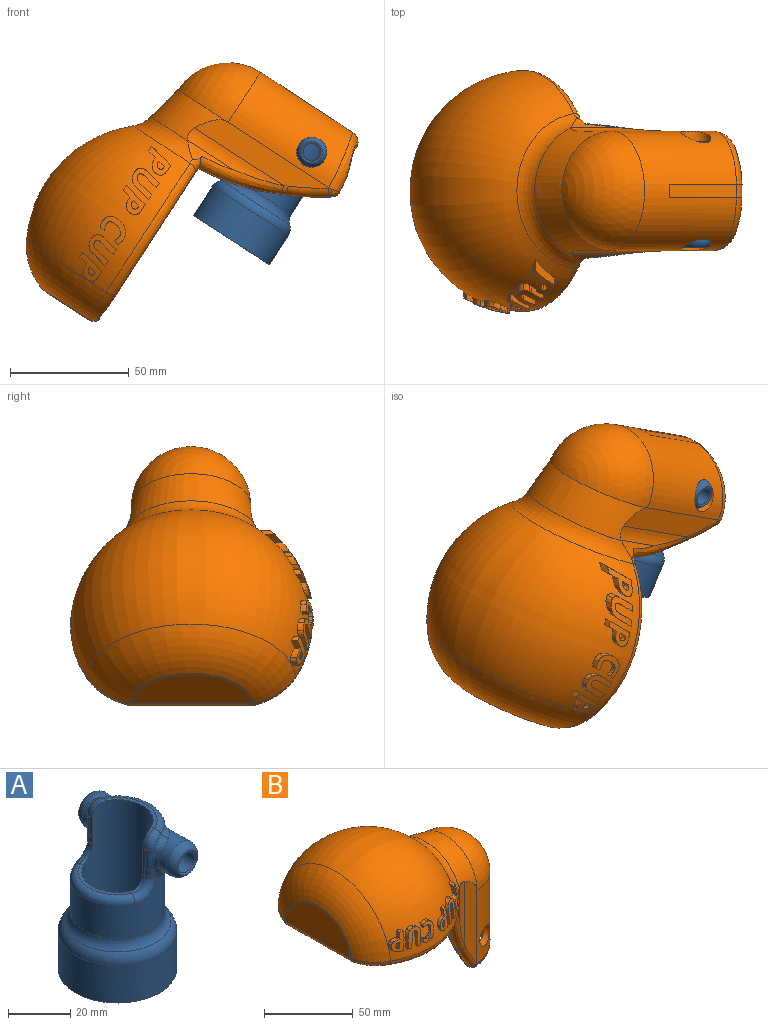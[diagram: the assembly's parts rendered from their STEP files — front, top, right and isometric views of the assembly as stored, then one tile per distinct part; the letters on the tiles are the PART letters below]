
ASSEMBLY  parts=2 mates=1
PART A: 61 faces, bbox 44.5x46.1x59 mm
  f0: cylinder r=6.35mm len=12.96mm, axis (0,1,0), area 175.7mm2, adj f33,f34,f35,f36,f37,f38,f39,f59
  f1: plane 27.88x27.32mm, normal (0,0,-1), area 165.8mm2, adj f3,f45,f47,f53,f54,f55
  f2: cylinder r=15.24mm len=33.18mm, axis (0,0,1), area 1735mm2, adj f14,f23,f24,f25,f26,f35,f50
  f3: cylinder r=11.43mm len=45.72mm, axis (0,0,1), area 2553.8mm2, adj f1,f4,f5,f6,f7,f10,f11,f12
  f4: plane 23.28x7.62mm, normal (0,0,1), area 34.8mm2, adj f3,f10,f11,f25
  f5: plane 23.28x7.62mm, normal (0,0,1), area 34.8mm2, adj f3,f12,f13,f14
  f6: plane 10.16x1.25mm, normal (-1,0,0), area 11.2mm2, adj f3,f11,f13,f18,f20,f22
  f7: plane 10.16x1.25mm, normal (-1,0,0), area 11.2mm2, adj f3,f10,f12,f17,f19,f21
  f8: cylinder r=6.35mm len=15.41mm, axis (0,-1,0), area 273.5mm2, adj f9,f26,f27,f28,f29,f30,f31,f32
  f9: torus R=2.54mm, axis (0,-1,0), area 137.8mm2, adj f8,f43
  f10: cylinder r=5.08mm len=5.08mm, axis (0,1,0), area 10.5mm2, adj f3,f4,f7,f23
  f11: cylinder r=5.08mm len=5.08mm, axis (0,1,0), area 10.5mm2, adj f3,f4,f6,f24
  f12: cylinder r=5.08mm len=5.08mm, axis (0,-1,0), area 7mm2, adj f3,f5,f7,f15
  f13: cylinder r=5.08mm len=5.08mm, axis (0,-1,0), area 7mm2, adj f3,f5,f6,f16
  f14: torus R=12.7mm, axis (0,0,-1), area 118.5mm2, adj f2,f5,f15,f16,f27,f33
  f15: bspline ~7.3x6.43mm, area 22.4mm2, adj f12,f14,f17,f34
  f16: bspline ~7.3x6.43mm, area 22.4mm2, adj f13,f14,f18,f29
  f17: cylinder r=2.54mm len=2.26mm, axis (0,0,1), area 0.7mm2, adj f7,f15,f19,f36
  f18: cylinder r=2.54mm len=2.26mm, axis (0,0,1), area 0.7mm2, adj f6,f16,f20,f31
  f19: bspline ~9x3.71mm, area 16.6mm2, adj f7,f17,f21,f38
  f20: bspline ~9x3.71mm, area 16.6mm2, adj f6,f18,f22,f32
  f21: cylinder r=2.54mm len=2.52mm, axis (0,0,1), area 7.9mm2, adj f7,f19,f23,f39
  f22: cylinder r=2.54mm len=2.52mm, axis (0,0,1), area 7.9mm2, adj f6,f20,f24,f30
  f23: bspline ~10.2x9.31mm, area 41.7mm2, adj f2,f10,f21,f25,f37
  f24: bspline ~10.2x9.31mm, area 41.7mm2, adj f2,f11,f22,f25,f28
  f25: torus R=12.7mm, axis (0,0,1), area 132.4mm2, adj f2,f4,f23,f24
  f26: bspline ~15.78x13.42mm, area 65mm2, adj f2,f8,f27,f28
  f27: bspline ~7.77x7.33mm, area 19.7mm2, adj f8,f14,f26,f29
  f28: bspline ~3.6x3.31mm, area 5mm2, adj f8,f24,f26,f30
  f29: bspline ~6.56x5.39mm, area 19.2mm2, adj f8,f16,f27,f31
  f30: bspline ~5.56x3.31mm, area 7.5mm2, adj f8,f22,f28,f32
  f31: bspline ~3.18x2.71mm, area 0.6mm2, adj f8,f18,f29,f32
  f32: bspline ~7.72x2.3mm, area 15.4mm2, adj f8,f20,f30,f31
  f33: bspline ~7.77x7.33mm, area 19.7mm2, adj f0,f14,f34,f35
  f34: bspline ~6.54x5.29mm, area 19.2mm2, adj f0,f15,f33,f36
  f35: bspline ~15.78x13.42mm, area 65mm2, adj f0,f2,f33,f37
  f36: bspline ~2.47x2.11mm, area 0.6mm2, adj f0,f17,f34,f38
  f37: bspline ~3.89x3.5mm, area 5mm2, adj f0,f23,f35,f39
  f38: bspline ~7.43x2.28mm, area 15.4mm2, adj f0,f19,f36,f39
  f39: bspline ~4.81x2.98mm, area 7.5mm2, adj f0,f21,f37,f38
  f40: cylinder r=15.24mm len=7.11mm, axis (0,0,1), area 47mm2, adj f42
  f41: cylinder r=3.81mm len=10.03mm, axis (0,-1,0), area 240.1mm2, adj f42,f43
  f42: bspline ~7.63x7.63mm, area 11.2mm2, adj f40,f41
  f43: torus R=4.32mm, axis (0,1,0), area 28.1mm2, adj f9,f41
  f44: cylinder r=14.02mm len=28.04mm, axis (0,0,1), area 244.3mm2, adj f46,f49,f52,f54
  f45: cylinder r=14.02mm len=28.04mm, axis (0,0,1), area 170.8mm2, adj f1,f46,f47,f53,f54
  f46: cylinder r=14.02mm len=28.04mm, axis (0,0,1), area 175.5mm2, adj f44,f45,f53,f54
  f47: cylinder r=14.02mm len=19.54mm, axis (0,0,1), area 18.5mm2, adj f1,f45,f53
  f48: cylinder r=19.05mm len=38.1mm, axis (0,0,1), area 1767.6mm2, adj f49,f51
  f49: plane 38.1x38.1mm, normal (0,0,-1), area 522.5mm2, adj f44,f48
  f50: torus R=20.32mm, axis (0,0,-1), area 454.3mm2, adj f2,f51
  f51: torus R=13.97mm, axis (0,0,-1), area 526mm2, adj f48,f50
  f52: plane 2.27x1.59mm, normal (0,-1,0), area 2.1mm2, adj f44,f53,f54,f55
  f53: bspline ~32.61x28.25mm, area 325.2mm2, adj f1,f45,f46,f47,f52,f55
  f54: bspline ~32.61x28.25mm, area 359.2mm2, adj f1,f44,f45,f46,f52,f55
  f55: bspline ~25.33x25.33mm, area 163.2mm2, adj f1,f52,f53,f54
  f56: cylinder r=15.24mm len=7.11mm, axis (0,0,1), area 47.1mm2, adj f57
  f57: bspline ~7.64x7.63mm, area 11.2mm2, adj f56,f58
  f58: cylinder r=3.81mm len=8.34mm, axis (0,1,0), area 199.5mm2, adj f57,f60
  f59: torus R=2.54mm, axis (0,1,0), area 137.8mm2, adj f0,f60
  f60: torus R=4.32mm, axis (0,-1,0), area 28.1mm2, adj f58,f59
PART B: 217 faces, bbox 157.1x102.9x107 mm
  f0: plane 67.87x24.74mm, normal (0,0,-1), area 166.8mm2, adj f145,f161,f174,f175,f176,f177,f188
  f1: cylinder r=81.7mm len=2.3mm, axis (0,1,0), area 0.2mm2, adj f153,f165,f194
  f2: cylinder r=81.7mm len=2.3mm, axis (0,1,0), area 0.2mm2, adj f151,f160,f202
  f3: revolved ~57.08x28.54mm, area 1079.3mm2, adj f4,f8,f10,f22,f146,f147,f148,f149
  f4: torus R=41.02mm, axis (1,0,0), area 709.4mm2, adj f3,f17,f146,f147,f168,f176
  f5: cylinder r=95.28mm len=36.91mm, axis (0,1,0), area 88.7mm2, adj f7,f155,f156,f189,f211,f212,f213,f216
  f6: plane 7.45x0.22mm, normal (0,0,-1), area 0.4mm2, adj f18,f190,f204,f214,f216
  f7: plane 67.88x24.74mm, normal (0,0,-1), area 166.8mm2, adj f5,f155,f168,f169,f170,f187,f189
  f8: plane 61.06x9.66mm, normal (0,1,0), area 482.8mm2, adj f3,f23,f148,f150,f156,f157
  f9: cylinder r=97.33mm len=16.92mm, axis (0,1,0), area 28.3mm2, adj f156,f157,f158,f159,f160,f204,f216
  f10: plane 61.05x9.66mm, normal (0,-1,0), area 482.8mm2, adj f3,f23,f149,f154,f162,f163
  f11: plane 23.45x18.02mm, normal (0,1,0), area 220.5mm2, adj f20,f26,f30,f140,f142,f191,f192,f193
  f12: cylinder r=97.33mm len=16.92mm, axis (0,1,0), area 28.3mm2, adj f162,f163,f164,f165,f166,f192,f210
  f13: plane 49.16x23.02mm, normal (1,0,0), area 873.9mm2, adj f139,f182
  f14: plane 51.98x22.46mm, normal (-1,0,0), area 884.5mm2, adj f167,f172
  f15: revolved ~87.08x61.63mm, area 8180.4mm2, adj f35,f139,f177,f178,f186,f187,f188,f189
  f16: plane 3.03x1.98mm, normal (-1,0,0), area 4.5mm2, adj f17,f81,f82,f114
  f17: revolved ~101.51x64.76mm, area 9394.4mm2, adj f4,f16,f37,f38,f39,f40,f41,f42
  f18: plane 23.45x18.02mm, normal (0,-1,0), area 220.5mm2, adj f6,f19,f25,f34,f143,f190,f201,f202
  f19: cylinder r=18.64mm len=7.12mm, axis (-1,0,0), area 25.2mm2, adj f18,f21,f25,f33
  f20: cylinder r=18.64mm len=7.12mm, axis (-1,0,0), area 25.2mm2, adj f11,f21,f26,f31
  f21: cylinder r=18.64mm len=37.28mm, axis (0,0,-1), area 1116.5mm2, adj f19,f20,f24,f32,f142,f143
  f22: sphere r=25.17mm, area 1990.7mm2, adj f3,f23
  f23: cylinder r=25.17mm len=50.39mm, axis (0,0,-1), area 3341.1mm2, adj f8,f10,f22,f25,f26,f27,f28,f151
  f24: sphere r=18.64mm, area 1091.3mm2, adj f21,f36
  f25: cylinder r=6.35mm len=12.7mm, axis (0,1,0), area 210.8mm2, adj f18,f19,f23,f33,f34
  f26: cylinder r=6.35mm len=12.7mm, axis (0,1,0), area 210.8mm2, adj f11,f20,f23,f30,f31
  f27: cylinder r=18.64mm len=5.71mm, axis (-1,0,0), area 0mm2, adj f23,f28
  f28: cylinder r=65.2mm len=33.92mm, axis (0,0,-1), area 193.1mm2, adj f23,f27,f151,f152,f153
  f29: cylinder r=51.61mm len=31.32mm, axis (0,0,-1), area 420.4mm2, adj f30,f31,f32,f33,f34,f197,f198,f199
  f30: cylinder r=12.7mm len=22.38mm, axis (0,0,-1), area 285.7mm2, adj f11,f26,f29,f31,f196
  f31: bspline ~12.67x11.58mm, area 94.4mm2, adj f20,f26,f29,f30,f32
  f32: bspline ~38.72x19.54mm, area 417.7mm2, adj f21,f29,f31,f33
  f33: bspline ~12.68x11.68mm, area 94.4mm2, adj f19,f25,f29,f32,f34
  f34: cylinder r=12.7mm len=22.38mm, axis (0,0,-1), area 285.7mm2, adj f18,f25,f29,f33,f200
  f35: torus R=38.79mm, axis (1,0,0), area 1101.1mm2, adj f15,f36,f141,f144,f188,f189,f205,f211
  f36: torus R=105.72mm, axis (1,0,0), area 1155mm2, adj f24,f35,f142,f143
  f37: torus R=19.04mm, axis (-1,0,0), area 2380.3mm2, adj f17,f170,f172,f174
  f38: extruded ~2.62x2.43mm, area 6.9mm2, adj f17,f39,f46,f117
  f39: extruded ~4.35x2.78mm, area 7.7mm2, adj f17,f38,f40,f117
  f40: plane 4.89x2.6mm, normal (0,0,-1), area 7.2mm2, adj f17,f39,f41,f117
  f41: plane 11.41x11.13mm, normal (0.98,0,-0.21), area 42.4mm2, adj f17,f40,f42,f117
  f42: plane 6.98x2.4mm, normal (0,0,1), area 10.4mm2, adj f17,f41,f43,f117
  f43: plane 6.77x3.99mm, normal (-0.98,0,0.2), area 15.7mm2, adj f17,f42,f44,f117
  f44: plane 4.09x0.66mm, normal (0,0,1), area 2.3mm2, adj f17,f43,f45,f117
  f45: extruded ~6.38x3.56mm, area 12.3mm2, adj f17,f44,f46,f117
  f46: extruded ~4.62x2.88mm, area 9.1mm2, adj f17,f38,f45,f117
  f47: plane 2.74x2.34mm, normal (0,0,-1), area 4.4mm2, adj f17,f48,f61,f116
  f48: plane 7.01x4.77mm, normal (0.98,0,-0.21), area 15.6mm2, adj f17,f47,f49,f116
  f49: extruded ~3.61x1.74mm, area 5mm2, adj f17,f48,f50,f116
  f50: extruded ~3.72x1.48mm, area 4.5mm2, adj f17,f49,f51,f116
  f51: extruded ~3x1.44mm, area 6.3mm2, adj f17,f50,f52,f116
  f52: extruded ~3.17x0.95mm, area 2.6mm2, adj f17,f51,f53,f116
  f53: plane 7.03x5.17mm, normal (-0.98,0,0.21), area 16.9mm2, adj f17,f52,f54,f116
  f54: plane 3.34x2.34mm, normal (0,0,-1), area 4.9mm2, adj f17,f53,f55,f116
  f55: plane 7.07x5.5mm, normal (0.98,0,-0.21), area 18mm2, adj f17,f54,f56,f116
  f56: extruded ~3.4x1.05mm, area 3.1mm2, adj f17,f55,f57,f116
  f57: extruded ~3.52x2.34mm, area 7.9mm2, adj f17,f56,f58,f116
  f58: extruded ~4.11x2.54mm, area 8.4mm2, adj f17,f57,f59,f116
  f59: extruded ~4.92x3.19mm, area 9.8mm2, adj f17,f58,f60,f116
  f60: extruded ~4.48x3.05mm, area 9mm2, adj f17,f59,f61,f116
  f61: plane 7.23x4.66mm, normal (-0.98,0,0.21), area 15.5mm2, adj f17,f47,f60,f116
  f62: extruded ~2.43x2.17mm, area 4.8mm2, adj f17,f63,f70,f115
  f63: extruded ~2.78x2.12mm, area 5.1mm2, adj f17,f62,f64,f115
  f64: plane 2.58x2.41mm, normal (0,0,-1), area 4.5mm2, adj f17,f63,f65,f115
  f65: plane 11.2x6.53mm, normal (0.98,0,-0.21), area 24.8mm2, adj f17,f64,f66,f115
  f66: plane 3.4x2.34mm, normal (0,0,1), area 6mm2, adj f17,f65,f67,f115
  f67: plane 4.21x3.97mm, normal (-0.98,0,0.2), area 9.7mm2, adj f17,f66,f68,f115
  f68: plane 2.4x0.66mm, normal (0,0,1), area 1.5mm2, adj f17,f67,f69,f115
  f69: extruded ~3.56x3.28mm, area 8.1mm2, adj f17,f68,f70,f115
  f70: extruded ~2.99x2.88mm, area 6.4mm2, adj f17,f62,f69,f115
  f71: extruded ~1.82x1.04mm, area 1.8mm2, adj f17,f72,f87,f114
  f72: extruded ~2x1.33mm, area 2.6mm2, adj f17,f71,f73,f114
  f73: plane 2.03x1.91mm, normal (-0.9,0,0.43), area 3.6mm2, adj f17,f72,f74,f114
  f74: extruded ~1.92x1.58mm, area 2.8mm2, adj f17,f73,f75,f114
  f75: extruded ~1.75x1.69mm, area 2.7mm2, adj f17,f74,f76,f114
  f76: extruded ~3.04x1.71mm, area 5.2mm2, adj f17,f75,f77,f114
  f77: extruded ~2.55x2.33mm, area 5.8mm2, adj f17,f76,f78,f114
  f78: extruded ~3.67x3.01mm, area 7.3mm2, adj f17,f77,f79,f114
  f79: extruded ~3.27x3.22mm, area 7.5mm2, adj f17,f78,f80,f114
  f80: extruded ~3x2.75mm, area 7.7mm2, adj f17,f79,f81,f114
  f81: extruded ~3.04x2.44mm, area 7.3mm2, adj f16,f17,f80,f114
  f82: extruded ~2.57x2.28mm, area 5.8mm2, adj f16,f17,f83,f114
  f83: extruded ~2.43x1.66mm, area 4mm2, adj f17,f82,f84,f114
  f84: extruded ~2.74x1.89mm, area 4.2mm2, adj f17,f83,f85,f114
  f85: extruded ~2.71x2.57mm, area 5.1mm2, adj f17,f84,f86,f114
  f86: extruded ~2.24x1.81mm, area 4.1mm2, adj f17,f85,f87,f114
  f87: extruded ~1.81x1.8mm, area 3.4mm2, adj f17,f71,f86,f114
  f88: plane 2.51x2.34mm, normal (0,0,-1), area 4.2mm2, adj f17,f89,f102,f113
  f89: plane 6.99x3.43mm, normal (0.98,0,-0.21), area 14.1mm2, adj f17,f88,f90,f113
  f90: extruded ~2.68x1.74mm, area 4.3mm2, adj f17,f89,f91,f113
  f91: extruded ~2.42x1.48mm, area 3.8mm2, adj f17,f90,f92,f113
  f92: extruded ~3.03x1.44mm, area 5.1mm2, adj f17,f91,f93,f113
  f93: extruded ~2.46x0.95mm, area 2.1mm2, adj f17,f92,f94,f113
  f94: plane 7.01x3.43mm, normal (-0.98,0,0.21), area 13.6mm2, adj f17,f93,f95,f113
  f95: plane 2.33x2.1mm, normal (0,0,-1), area 3.9mm2, adj f17,f94,f96,f113
  f96: plane 7.04x3.46mm, normal (0.98,0,-0.21), area 13.4mm2, adj f17,f95,f97,f113
  f97: extruded ~2.47x1.05mm, area 2.2mm2, adj f17,f96,f98,f113
  f98: extruded ~3.28x2.34mm, area 5.8mm2, adj f17,f97,f99,f113
  f99: extruded ~3.22x2.54mm, area 6.6mm2, adj f17,f98,f100,f113
  f100: extruded ~3.19x2.78mm, area 8.4mm2, adj f17,f99,f101,f113
  f101: extruded ~3.06x3.05mm, area 8.4mm2, adj f17,f100,f102,f113
  f102: plane 7.22x3.52mm, normal (-0.98,0,0.21), area 15.1mm2, adj f17,f88,f101,f113
  f103: extruded ~3.45x2.43mm, area 6.3mm2, adj f17,f104,f111,f112
  f104: extruded ~3.63x2.78mm, area 6.3mm2, adj f17,f103,f105,f112
  f105: plane 3.05x2.59mm, normal (0,0,-1), area 5.1mm2, adj f17,f104,f106,f112
  f106: plane 11.19x5.03mm, normal (0.98,0,-0.21), area 25.8mm2, adj f17,f105,f107,f112
  f107: plane 3.62x2.34mm, normal (0,0,1), area 6.3mm2, adj f17,f106,f108,f112
  f108: plane 3.97x3.9mm, normal (-0.98,0,0.2), area 10.5mm2, adj f17,f107,f109,f112
  f109: plane 2.76x0.66mm, normal (0,0,1), area 1.6mm2, adj f17,f108,f110,f112
  f110: extruded ~3.89x3.56mm, area 9.6mm2, adj f17,f109,f111,f112
  f111: extruded ~2.88x2.74mm, area 8.3mm2, adj f17,f103,f110,f112
  f112: revolved ~11.85x8.65mm, area 53.2mm2, adj f103,f104,f105,f106,f107,f108,f109,f110
  f113: revolved ~11.76x9.83mm, area 57mm2, adj f88,f89,f90,f91,f92,f93,f94,f95
  f114: revolved ~11.49x9.22mm, area 42.2mm2, adj f16,f71,f72,f73,f74,f75,f76,f77
  f115: revolved ~12.08x8.65mm, area 50.6mm2, adj f62,f63,f64,f65,f66,f67,f68,f69
  f116: revolved ~13.03x9.83mm, area 60.7mm2, adj f47,f48,f49,f50,f51,f52,f53,f54
  f117: revolved ~14.88x10.35mm, area 61.6mm2, adj f38,f39,f40,f41,f42,f43,f44,f45
  f118: revolved ~3.65x2.75mm, area 7.5mm2, adj f119,f120,f121,f122,f123,f124
  f119: plane 2.53x0.43mm, normal (0,0,-1), area 1mm2, adj f112,f118,f120,f124
  f120: extruded ~2.99x1.7mm, area 4.3mm2, adj f112,f118,f119,f121
  f121: extruded ~2.47x1.41mm, area 3.8mm2, adj f112,f118,f120,f122
  f122: extruded ~3.28x1.48mm, area 5.2mm2, adj f112,f118,f121,f123
  f123: plane 2.39x0.56mm, normal (0,0,1), area 1.2mm2, adj f112,f118,f122,f124
  f124: plane 3.31x2.85mm, normal (-0.98,0,0.21), area 7.5mm2, adj f112,f118,f119,f123
  f125: revolved ~3.59x2.75mm, area 6.8mm2, adj f126,f127,f128,f129,f130,f131
  f126: plane 2.18x0.43mm, normal (0,0,-1), area 0.9mm2, adj f115,f125,f127,f131
  f127: extruded ~2.59x1.7mm, area 3.7mm2, adj f115,f125,f126,f128
  f128: extruded ~2.45x1.41mm, area 3.1mm2, adj f115,f125,f127,f129
  f129: extruded ~1.89x1.48mm, area 4.3mm2, adj f115,f125,f128,f130
  f130: plane 1.97x0.56mm, normal (0,0,1), area 1mm2, adj f115,f125,f129,f131
  f131: plane 3.31x3.01mm, normal (-0.98,0,0.21), area 6.6mm2, adj f115,f125,f126,f130
  f132: revolved ~4.52x3.39mm, area 8.6mm2, adj f133,f134,f135,f136,f137,f138
  f133: plane 3.63x0.43mm, normal (0,0,-1), area 1.4mm2, adj f117,f132,f134,f138
  f134: extruded ~4.64x1.7mm, area 5.7mm2, adj f117,f132,f133,f135
  f135: extruded ~3.83x1.41mm, area 4.6mm2, adj f117,f132,f134,f136
  f136: extruded ~3.52x1.48mm, area 6.5mm2, adj f117,f132,f135,f137
  f137: plane 3.31x0.56mm, normal (0,0,1), area 1.6mm2, adj f117,f132,f136,f138
  f138: plane 4.77x3.32mm, normal (-0.98,0,0.21), area 10.4mm2, adj f117,f132,f133,f137
  f139: torus R=24.63mm, axis (-1,0,0), area 1137.6mm2, adj f13,f15,f179,f180,f181,f183,f184,f185
  f140: plane 7.45x0.22mm, normal (0,0,-1), area 0.4mm2, adj f11,f191,f192,f207,f210
  f141: cylinder r=21.32mm len=14.75mm, axis (0,0,-1), area 23.2mm2, adj f35,f142,f206,f208
  f142: cylinder r=87.42mm len=37.15mm, axis (0,0,-1), area 633.9mm2, adj f11,f21,f36,f141,f191,f208
  f143: cylinder r=87.42mm len=37.15mm, axis (0,0,-1), area 633.9mm2, adj f18,f21,f36,f144,f190,f213
  f144: cylinder r=21.32mm len=14.75mm, axis (0,0,-1), area 23.2mm2, adj f35,f143,f212,f213
  f145: cylinder r=95.28mm len=36.91mm, axis (0,1,0), area 88.7mm2, adj f0,f161,f162,f188,f205,f206,f208,f210
  f146: cylinder r=24.08mm len=23.11mm, axis (0,0,-1), area 60.2mm2, adj f3,f4,f149,f161,f176
  f147: cylinder r=24.08mm len=23.11mm, axis (0,0,-1), area 60.2mm2, adj f3,f4,f148,f155,f168
  f148: cylinder r=12.7mm len=44.61mm, axis (0,0,-1), area 206.1mm2, adj f3,f8,f147,f155
  f149: cylinder r=12.7mm len=44.61mm, axis (0,0,-1), area 206.1mm2, adj f3,f10,f146,f161
  f150: torus R=76.62mm, axis (0,-1,0), area 0.2mm2, adj f8,f151,f158
  f151: bspline ~27.91x24.63mm, area 180.3mm2, adj f2,f23,f28,f150,f152,f159,f199,f200
  f152: bspline ~14.23x5.03mm, area 31.9mm2, adj f28,f151,f153,f198
  f153: bspline ~27.91x24.63mm, area 180.3mm2, adj f1,f23,f28,f152,f154,f166,f195,f196
  f154: torus R=76.62mm, axis (0,1,0), area 0.2mm2, adj f10,f153,f164
  f155: bspline ~44.5x15.37mm, area 267.7mm2, adj f5,f7,f147,f148,f156,f168
  f156: torus R=91.47mm, axis (0,-1,0), area 11.8mm2, adj f5,f8,f9,f155,f157,f216
  f157: torus R=93.52mm, axis (0,-1,0), area 103.9mm2, adj f8,f9,f156,f158
  f158: bspline ~4.4x4.19mm, area 5.7mm2, adj f9,f150,f157,f159
  f159: bspline ~6.05x4.52mm, area 19.8mm2, adj f9,f151,f158,f160
  f160: cylinder r=3.81mm len=3.38mm, axis (0,1,0), area 0.7mm2, adj f2,f9,f159,f203
  f161: bspline ~44.5x15.37mm, area 267.7mm2, adj f0,f145,f146,f149,f162,f176
  f162: torus R=91.47mm, axis (0,1,0), area 11.9mm2, adj f10,f12,f145,f161,f163,f210
  f163: torus R=93.52mm, axis (0,1,0), area 103.9mm2, adj f10,f12,f162,f164
  f164: bspline ~4.4x4.19mm, area 5.7mm2, adj f12,f154,f163,f166
  f165: cylinder r=3.81mm len=3.38mm, axis (0,1,0), area 0.7mm2, adj f1,f12,f166,f193
  f166: bspline ~6.05x4.52mm, area 19.8mm2, adj f12,f153,f164,f165
  f167: cylinder r=3.81mm len=51.98mm, axis (0,1,0), area 207.6mm2, adj f14,f171,f173,f181,f182,f183
  f168: bspline ~10.76x9.11mm, area 35.5mm2, adj f4,f7,f147,f155,f169
  f169: bspline ~70.75x22.46mm, area 437.5mm2, adj f7,f17,f168,f170
  f170: bspline ~22.72x18.89mm, area 113.9mm2, adj f7,f37,f169,f171,f185,f186
  f171: sphere r=3.81mm, area 3.8mm2, adj f167,f170,f172,f184
  f172: torus R=26.27mm, axis (-1,0,0), area 84.9mm2, adj f14,f37,f171,f173
  f173: sphere r=3.81mm, area 3.8mm2, adj f167,f172,f174,f180
  f174: bspline ~22.72x18.89mm, area 113.9mm2, adj f0,f37,f173,f175,f178,f179
  f175: bspline ~70.75x22.46mm, area 437.5mm2, adj f0,f17,f174,f176
  f176: bspline ~10.76x9.11mm, area 35.5mm2, adj f0,f4,f146,f161,f175
  f177: bspline ~67.29x17.84mm, area 126.1mm2, adj f0,f15,f178,f188
  f178: bspline ~8.41x5.39mm, area 7.6mm2, adj f15,f174,f177,f179
  f179: bspline ~12.28x8.45mm, area 30.4mm2, adj f139,f174,f178,f180
  f180: bspline ~2.17x2.03mm, area 1.2mm2, adj f139,f173,f179,f181
  f181: bspline ~3.4x2.2mm, area 3.5mm2, adj f139,f167,f180,f182
  f182: cylinder r=1.27mm len=49.16mm, axis (0,1,0), area 130.8mm2, adj f13,f167,f181,f183
  f183: bspline ~3.4x2.2mm, area 3.5mm2, adj f139,f167,f182,f184
  f184: bspline ~2.17x2.03mm, area 1.2mm2, adj f139,f171,f183,f185
  f185: bspline ~12.02x7.94mm, area 30.4mm2, adj f139,f170,f184,f186
  f186: bspline ~7.82x5mm, area 7.6mm2, adj f15,f170,f185,f187
  f187: bspline ~66.44x18.32mm, area 126.1mm2, adj f7,f15,f186,f189
  f188: bspline ~11.97x10.32mm, area 21.8mm2, adj f0,f15,f35,f145,f177,f205
  f189: bspline ~11.97x10.32mm, area 21.8mm2, adj f5,f7,f15,f35,f187,f211
  f190: torus R=87.16mm, axis (0,0,1), area 3.6mm2, adj f6,f18,f143,f214
  f191: torus R=87.16mm, axis (0,0,1), area 3.6mm2, adj f11,f140,f142,f207
  f192: torus R=96.06mm, axis (0,1,0), area 37.9mm2, adj f11,f12,f140,f193,f210
  f193: torus R=2.54mm, axis (0,1,0), area 6.8mm2, adj f11,f165,f192,f194
  f194: torus R=80.43mm, axis (0,1,0), area 4.6mm2, adj f1,f11,f193,f195
  f195: bspline ~5.98x2.24mm, area 8.6mm2, adj f11,f153,f194,f196
  f196: bspline ~15.46x13.78mm, area 56.9mm2, adj f30,f153,f195,f197
  f197: bspline ~7.92x2.82mm, area 14.8mm2, adj f29,f153,f196,f198
  f198: bspline ~12.73x2.29mm, area 12.1mm2, adj f29,f152,f197,f199
  f199: bspline ~7.92x2.82mm, area 14.8mm2, adj f29,f151,f198,f200
  f200: bspline ~15.76x13.04mm, area 56.9mm2, adj f34,f151,f199,f201
  f201: bspline ~6.93x2.34mm, area 8.6mm2, adj f18,f151,f200,f202
  f202: torus R=80.43mm, axis (0,1,0), area 4.6mm2, adj f2,f18,f201,f203
  f203: torus R=2.54mm, axis (0,1,0), area 6.8mm2, adj f18,f160,f202,f204
  f204: torus R=96.06mm, axis (0,1,0), area 37.9mm2, adj f6,f9,f18,f203,f216
  f205: bspline ~5.6x1.5mm, area 1mm2, adj f35,f145,f188,f206
  f206: bspline ~21.28x3.8mm, area 20.9mm2, adj f141,f145,f205,f208
  f207: bspline ~1.15x0.49mm, area 0.2mm2, adj f140,f191,f208,f209
  f208: bspline ~33.53x14.17mm, area 45mm2, adj f141,f142,f145,f206,f207,f209
  f209: bspline ~1.18x1.16mm, area 0.2mm2, adj f207,f208,f210
  f210: cylinder r=1.27mm len=3.07mm, axis (0,1,0), area 0.7mm2, adj f12,f140,f145,f162,f192,f209
  f211: bspline ~5.6x1.5mm, area 1mm2, adj f5,f35,f189,f212
  f212: bspline ~21.28x3.8mm, area 20.9mm2, adj f5,f144,f211,f213
  f213: bspline ~33.53x14.17mm, area 45mm2, adj f5,f143,f144,f212,f214,f215
  f214: bspline ~1.15x0.49mm, area 0.2mm2, adj f6,f190,f213,f215
  f215: bspline ~1.18x1.16mm, area 0.2mm2, adj f213,f214,f216
  f216: cylinder r=1.27mm len=3.07mm, axis (0,1,0), area 0.7mm2, adj f5,f6,f9,f156,f204,f215
PLACE A rot(axis=(0,1,0),33deg) t=(-39.71,7,8.42)mm
PLACE B rot(axis=(0,-1,0),57deg) t=(13.34,7.28,7.42)mm
MATE pin_slot B.f25 <-> A.f0  axis (0,1,0) through (-12.86,-13.18,34.72)mm
